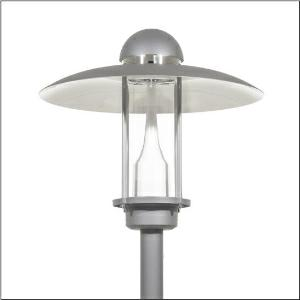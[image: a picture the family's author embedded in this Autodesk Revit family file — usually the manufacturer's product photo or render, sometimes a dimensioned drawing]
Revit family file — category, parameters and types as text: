
# Revit family: city-light_elegance_iq___p1_0a_5xa5265lf14h_79ad
name_source: partatom
category: Lighting Fixtures
units: mm (PartAtom-declared; Revit-internal decimal feet)

## family parameters
Cut with Voids When Loaded = No
Host = Face
Light Source = No
Part Type = Normal
Room Calculation Point = No
Round Connector Dimension = Use Diameter
Shared = No

## types (1)
- --- (1 x LED, 1440 lm, 10 W, 4000K)
    Apparent Load = 10 VA
    CIE Flux Codes = 32 62 91 97 100
    Color Rendering = 70
    Color Temperature = 4000K
    Default Elevation = 1800 mm
    Description = City-Light Elegance iQ, mast luminaire, Module 540 iQ-SR, primary light control with 3 zone facetted reflector, of plastic, silver coated, highly specular, structured, primary optical cover: cover, of PMMA, transparent, light distribution: P1.0a, light emission: direct distribution, primary light characteristic: strongly asymmetric, installation type: post-top, LED, High Power LED, rated luminous flux: 1.440lm, luminous efficacy: 144lm/W, light colour: 740, colour temperature: 4000K, control gear: ECG iQ, control: pre-setting: logarithmic dimming characteristic, Street-Remote, Auto-Match, Temp-Guard, Lumen-Switch, Night-Set, Smart-Wire, Light-Fading, Desk-Remote (wireless, voltage-free reading and setting of iQ features in the workshop via application-optimized NFC function/RFID function), optimised constant luminous flux control (CLO 2.0), with terminal, 6-pole, max. 2.5mm², mains connection: 230..240V, AC, 50/60Hz, start of lifetime: 10W, end of service life: 10W, reduction: 5W, luminaire housing, upper part, of aluminium, coated, Siteco® metallic grey (DB 702S), diameter: 750mm, height: 675mm, spigot size: d x l = 76 x 70mm (post-top) | with reducer (optional accessory) 60 x 70mm, post-top mast mounting element, of diecast aluminium, coated, Siteco® metallic grey (DB 702S), Module 540 iQ-SR, traffic white (RAL 9016), equipment: standard, protection rating (complete): IP65, insulation class (complete): insulation class II (safety insulation), certification: CE, ENEC, VDE, packaging unit: 1 piece

Light Distribution: P1.0a
    Height = 675 mm
    Lamp = 1 x LED
    Lamp Light Flux = 1440 lm
    Lamp Power = 10 W
    Lamp count = 1
    Length = 750 mm
    Luminous efficacy = 144 lm/W
    Manufacturer = Siteco
    ModVariant = No
    Model = 5XA5265LF14H
    Number of Poles = 1
    OnlyDefault = Yes
    Power Factor = 1
    Product Name = City-Light Elegance iQ | P1.0a
    Product group = mast luminaire | pylon top
    ProductGroupID = 6100
    Protection Class = Protection class II
    Protection Degree = IP 65
    RLX_Detail_Level = 1
    RLX_Emergency_Light_Flux = 0 lm
    RLX_Emergency_Type = 0
    RLX_Emergency_Type_DB = No
    RlxData = <blob elided: 106101 chars, md5=e572adcc>
    Socket = socket
    Standby Power = 0 W
    System Light Flux = 1440 lm
    System Power = 10 W
    Type Comments = factory setting: luminous flux: 100 % | dim-lin: 254 | 401 mA
    Type Image = l_1006912.jpg
    URL = http://relux.com
    VarID = @adj_130051
    Voltage = 0 V
    Weight = 0.00 kg
    Width = 0 mm  [stored 0 ft]

note: [stored X ft] marks values corroborated as IEEE doubles in the binary element streams (Revit-internal decimal feet)

## geometry (parser evidence)
native form markers: Blend x4, Sweep x11
no freeform markers — native parametric forms only
